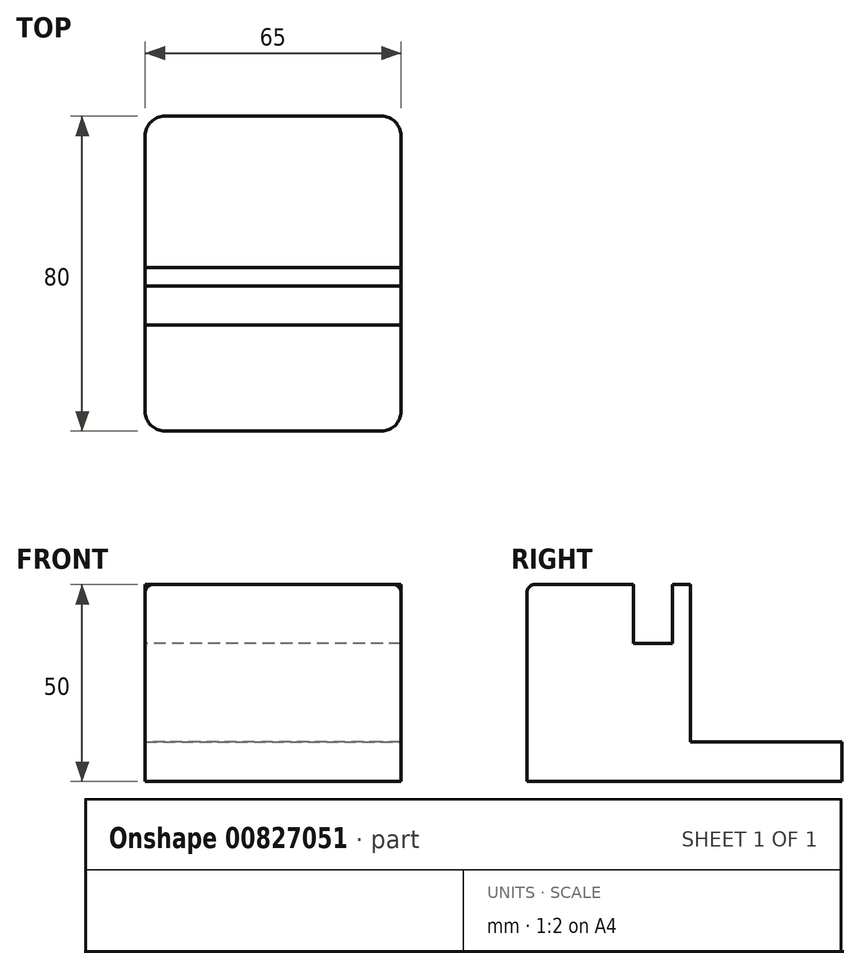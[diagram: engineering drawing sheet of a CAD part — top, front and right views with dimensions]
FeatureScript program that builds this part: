
annotation { "Feature Type Name" : "Feature", "Feature Type Description" : "" }
export const myFeature = defineFeature(function(context is Context, id is Id, definition is map)
    precondition{}
    {
        {
            var Q0;
            Q0=qCreatedBy(makeId("Top.planeOp"),FACE);
            var sketch = newSketch(context, id + "F0", { "sketchPlane" : qUnion([Q0])});
            skLineSegment(sketch, "E0.bottom", {"start": v(27.5, 40) * mm, "end": v(-27.5, 40) * mm});
            skLineSegment(sketch, "E0.top", {"start": v(27.5, -40) * mm, "end": v(-27.5, -40) * mm});
            skPoint(sketch, "E0.middle", {"position": v(0, 0) * mm});
            skLineSegment(sketch, "E1", {"start": v(-32.5, -13) * mm, "end": v(-32.5, -3.1) * mm});
            skLineSegment(sketch, "E2", {"start": v(-32.5, 35) * mm, "end": v(-32.5, -3.1) * mm});
            skLineSegment(sketch, "E3", {"start": v(-32.5, -13) * mm, "end": v(-32.5, -35) * mm});
            skPoint(sketch, "E4.visualSharp", {"position": v(-32.5, -40) * mm});
            skArc(sketch, "E4.filletArc", {"start": v(-32.5, -35) * mm, "mid": v(-31.04, -38.54) * mm, "end": v(-27.5, -40) * mm});
            skPoint(sketch, "E5.visualSharp", {"position": v(32.5, -40) * mm});
            skArc(sketch, "E5.filletArc", {"start": v(27.5, -40) * mm, "mid": v(31.04, -38.54) * mm, "end": v(32.5, -35) * mm});
            skPoint(sketch, "E6.visualSharp", {"position": v(32.5, 40) * mm});
            skArc(sketch, "E6.filletArc", {"start": v(32.5, 35) * mm, "mid": v(31.04, 38.54) * mm, "end": v(27.5, 40) * mm});
            skPoint(sketch, "E7.visualSharp", {"position": v(-32.5, 40) * mm});
            skArc(sketch, "E7.filletArc", {"start": v(-27.5, 40) * mm, "mid": v(-31.04, 38.54) * mm, "end": v(-32.5, 35) * mm});
            skLineSegment(sketch, "E8", {"start": v(32.5, -13) * mm, "end": v(32.5, -35) * mm});
            skLineSegment(sketch, "E9", {"start": v(32.5, -13) * mm, "end": v(32.5, -3.1) * mm});
            skLineSegment(sketch, "E10", {"start": v(-32.5, -3.1) * mm, "end": v(32.5, -3.1) * mm});
            skLineSegment(sketch, "E11", {"start": v(32.5, -13) * mm, "end": v(-32.5, -13) * mm});
            skLineSegment(sketch, "E12", {"start": v(32.5, -3.1) * mm, "end": v(32.5, 1.5) * mm});
            skLineSegment(sketch, "E13", {"start": v(32.5, 1.5) * mm, "end": v(-32.5, 1.5) * mm});
            skLineSegment(sketch, "E14", {"start": v(32.5, 35) * mm, "end": v(32.5, 1.5) * mm});
            skSolve(sketch);
        }
        {
            var Q0;
            Q0=makeQuery(id+"F0.imprint","IMPRINT",FACE,{"disambiguationData":[TD([[makeQuery(id+"F0.imprint","IMPRINT",EDGE,{"derivedFrom":sQuery(id+"F0.wireOp",EDGE,"E0.bottom")}),1.0]])]});
            var Q1;
            {var subQ0=sQuery(id+"F0.wireOp",EDGE,"E10");Q1=makeQuery(id+"F0.imprint","IMPRINT",FACE,{"disambiguationData":[TD([[makeQuery(id+"F0.imprint","IMPRINT",EDGE,{"derivedFrom":subQ0}),1.0]])]});}
            var Q2;
            Q2=makeQuery(id+"F0.imprint","IMPRINT",FACE,{"disambiguationData":[TD([[makeQuery(id+"F0.imprint","IMPRINT",EDGE,{"derivedFrom":sQuery(id+"F0.wireOp",EDGE,"E1")}),-1.0]])]});
            var Q3;
            Q3=makeQuery(id+"F0.imprint","IMPRINT",FACE,{"disambiguationData":[TD([[makeQuery(id+"F0.imprint","IMPRINT",EDGE,{"derivedFrom":sQuery(id+"F0.wireOp",EDGE,"E0.top")}),-1.0]])]});
            extrude(context, id + "F1", {"entities" : qUnion([Q0, Q1, Q2, Q3]), "depth" : 10 * mm, "offsetDistance" : 25 * mm});
        }
        {
            var Q0;
            {var subQ0=sQuery(id+"F0.wireOp",EDGE,"E10");Q0=makeQuery(id+"F0.imprint","IMPRINT",FACE,{"disambiguationData":[TD([[makeQuery(id+"F0.imprint","IMPRINT",EDGE,{"derivedFrom":subQ0}),1.0]])]});}
            var Q1;
            Q1=makeQuery(id+"F0.imprint","IMPRINT",FACE,{"disambiguationData":[TD([[makeQuery(id+"F0.imprint","IMPRINT",EDGE,{"derivedFrom":sQuery(id+"F0.wireOp",EDGE,"E0.top")}),-1.0]])]});
            extrude(context, id + "F2", {"entities" : qUnion([Q0, Q1]), "operationType" : NewBodyOperationType.ADD, "depth" : 50 * mm, "offsetDistance" : 25 * mm});
        }
        {
            var Q0;
            Q0=makeQuery(id+"F0.imprint","IMPRINT",FACE,{"disambiguationData":[TD([[makeQuery(id+"F0.imprint","IMPRINT",EDGE,{"derivedFrom":sQuery(id+"F0.wireOp",EDGE,"E1")}),-1.0]])]});
            extrude(context, id + "F3", {"entities" : qUnion([Q0]), "operationType" : NewBodyOperationType.ADD, "depth" : 35 * mm, "offsetDistance" : 25 * mm});
        }
        {
            var Q0;
            Q0=makeQuery(id+"F2.opExtrude","CAP_EDGE",EDGE,{"disambiguationData":[OSD([sQuery(id+"F0.wireOp",EDGE,"E3")])],"isStart":false});
            var Q1;
            Q1=makeQuery(id+"F2.opExtrude","CAP_EDGE",EDGE,{"disambiguationData":[OSD([sQuery(id+"F0.wireOp",EDGE,"E8")])],"isStart":false});
            fillet(context, id + "F4", {"entities" : qUnion([Q0, Q1]), "radius" : 2 * mm, "tangentPropagation" : true, "allowEdgeOverflow" : false});
        }
    });
